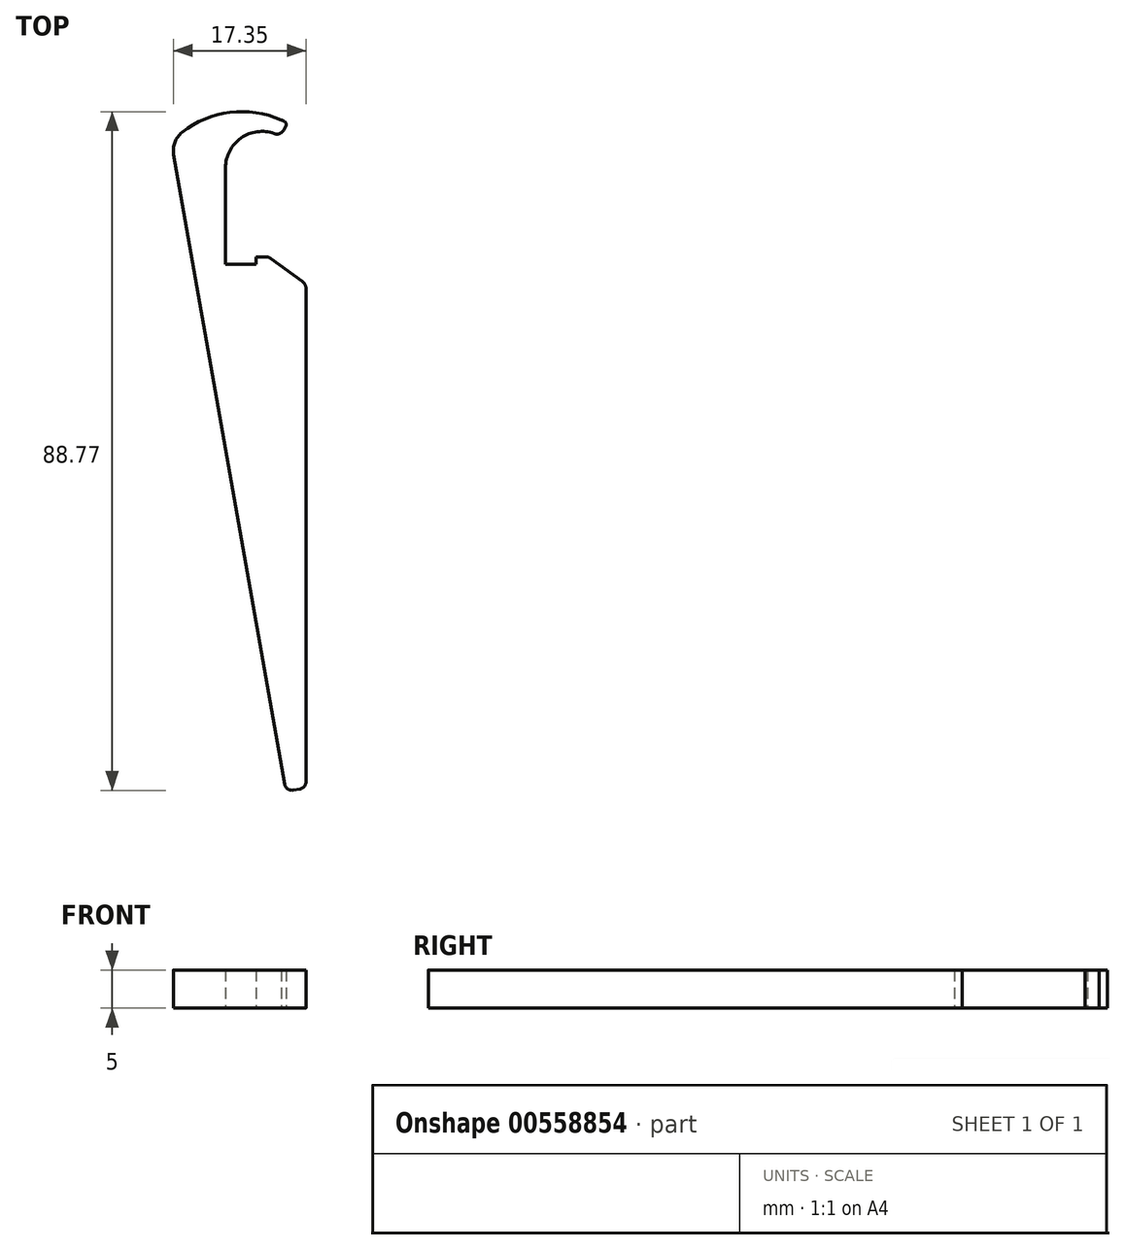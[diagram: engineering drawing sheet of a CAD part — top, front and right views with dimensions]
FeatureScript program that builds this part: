
annotation { "Feature Type Name" : "Feature", "Feature Type Description" : "" }
export const myFeature = defineFeature(function(context is Context, id is Id, definition is map)
    precondition{}
    {
        {
            var Q0;
            Q0=qCreatedBy(makeId("Top.planeOp"),FACE);
            var sketch = newSketch(context, id + "F0", { "sketchPlane" : qUnion([Q0])});
            skArc(sketch, "E0", {"start": v(-30, 17.9) * mm, "mid": v(-34.36, 17.33) * mm, "end": v(-36.38, 13.44) * mm});
            skLineSegment(sketch, "E1", {"start": v(-36.38, 13.44) * mm, "end": v(-36.38, 0.79) * mm});
            skLineSegment(sketch, "E2", {"start": v(-36.38, 0.79) * mm, "end": v(-32.38, 0.79) * mm});
            skLineSegment(sketch, "E3", {"start": v(-32.38, 0.79) * mm, "end": v(-32.38, 1.79) * mm});
            skLineSegment(sketch, "E4", {"start": v(-31.63, 13.44) * mm, "end": v(-26.88, 13.44) * mm, "construction": true});
            skLineSegment(sketch, "E5", {"start": v(-28.8, 18.34) * mm, "end": v(-28.52, 18.83) * mm});
            skArc(sketch, "E6", {"start": v(-28.74, 19.54) * mm, "mid": v(-28.9, 19.61) * mm, "end": v(-29.08, 19.69) * mm});
            skLineSegment(sketch, "E7", {"start": v(-40.6, 0.62) * mm, "end": v(-28.64, -67.16) * mm});
            skLineSegment(sketch, "E8", {"start": v(-27.48, -67.97) * mm, "end": v(-26.68, -67.83) * mm});
            skLineSegment(sketch, "E9", {"start": v(-25.86, -66.85) * mm, "end": v(-25.86, -2.4) * mm});
            skLineSegment(sketch, "E10", {"start": v(-25.86, 0.48) * mm, "end": v(-25.86, 0.79) * mm});
            skLineSegment(sketch, "E11", {"start": v(-31.1, 1.79) * mm, "end": v(-32.38, 1.79) * mm});
            skLineSegment(sketch, "E12.trimOffspring", {"start": v(-24.88, 13.44) * mm, "end": v(-24.13, 13.44) * mm, "construction": true});
            skPoint(sketch, "E13.visualSharp", {"position": v(-40.62, 0.79) * mm});
            skArc(sketch, "E13.filletArc", {"start": v(-40.6, 0.96) * mm, "mid": v(-40.6, 0.79) * mm, "end": v(-40.6, 0.62) * mm});
            skPoint(sketch, "E14.visualSharp", {"position": v(-28.47, -68.15) * mm});
            skArc(sketch, "E14.filletArc", {"start": v(-28.64, -67.16) * mm, "mid": v(-28.23, -67.8) * mm, "end": v(-27.48, -67.97) * mm});
            skPoint(sketch, "E15.visualSharp", {"position": v(-25.86, -67.69) * mm});
            skArc(sketch, "E15.filletArc", {"start": v(-26.68, -67.83) * mm, "mid": v(-26.1, -67.5) * mm, "end": v(-25.86, -66.85) * mm});
            skPoint(sketch, "E16.visualSharp", {"position": v(-25.86, 1.79) * mm});
            skLineSegment(sketch, "E17", {"start": v(-40.6, 0.62) * mm, "end": v(-43.16, 15.19) * mm});
            skArc(sketch, "E18", {"start": v(-28.26, 19.28) * mm, "mid": v(-35.34, 20.73) * mm, "end": v(-42.07, 18.06) * mm});
            skPoint(sketch, "E18.second.point", {"position": v(-43.44, 16.8) * mm});
            skPoint(sketch, "E18.third.point", {"position": v(-21.64, 9.32) * mm});
            skArc(sketch, "E19.filletArc", {"start": v(-42.07, 18.06) * mm, "mid": v(-43, 16.78) * mm, "end": v(-43.16, 15.19) * mm});
            skArc(sketch, "E20.filletArc", {"start": v(-30, 17.9) * mm, "mid": v(-29.33, 17.9) * mm, "end": v(-28.8, 18.34) * mm});
            skPoint(sketch, "E21.visualSharp", {"position": v(-28.26, 19.28) * mm});
            skArc(sketch, "E21.filletArc", {"start": v(-28.52, 18.83) * mm, "mid": v(-28.47, 19.23) * mm, "end": v(-28.74, 19.54) * mm});
            skLineSegment(sketch, "E22", {"start": v(-30.51, 1.6) * mm, "end": v(-26.35, -1.44) * mm});
            skPoint(sketch, "E23.visualSharp", {"position": v(-30.78, 1.79) * mm});
            skArc(sketch, "E23.filletArc", {"start": v(-30.51, 1.6) * mm, "mid": v(-30.8, 1.74) * mm, "end": v(-31.1, 1.79) * mm});
            skPoint(sketch, "E24.visualSharp", {"position": v(-25.86, -1.8) * mm});
            skArc(sketch, "E24.filletArc", {"start": v(-25.86, -2.4) * mm, "mid": v(-25.99, -1.86) * mm, "end": v(-26.35, -1.44) * mm});
            skSolve(sketch);
        }
        {
            var Q0;
            Q0 = qSketchRegion(id + "F0", true);
            extrude(context, id + "F1", {"entities" : qUnion([Q0]), "depth" : 5 * mm, "offsetDistance" : 25 * mm});
        }
    });
